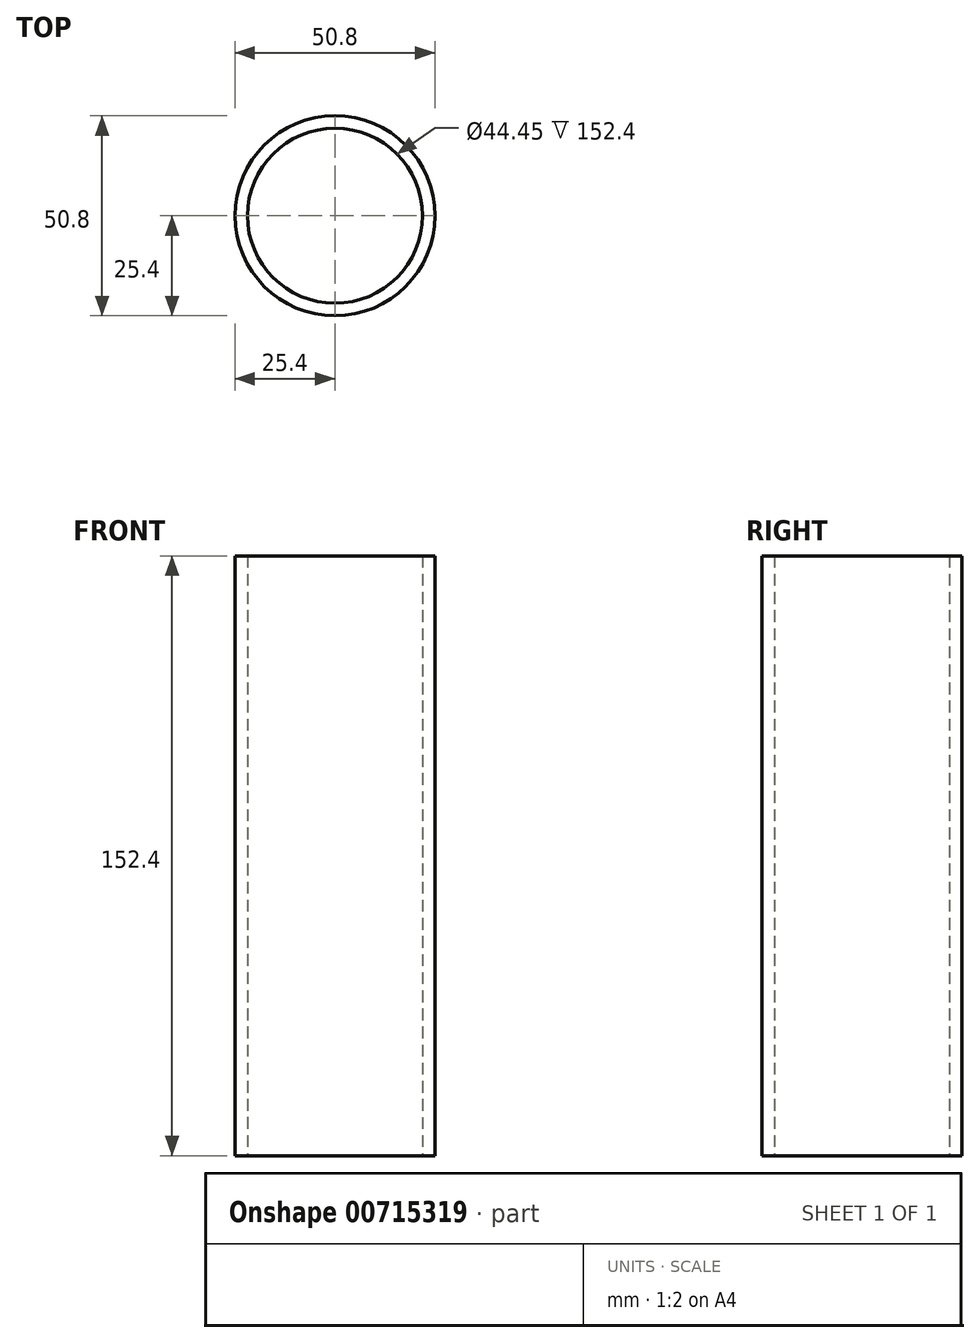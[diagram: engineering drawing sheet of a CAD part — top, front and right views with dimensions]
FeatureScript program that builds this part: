
annotation { "Feature Type Name" : "Feature", "Feature Type Description" : "" }
export const myFeature = defineFeature(function(context is Context, id is Id, definition is map)
    precondition{}
    {
        {
            var Q0;
            Q0=qCreatedBy(makeId("Top.planeOp"),FACE);
            var sketch = newSketch(context, id + "F0", { "sketchPlane" : qUnion([Q0])});
            skCircle(sketch, "E0", {"center": v(0, 0) * mm, "radius": 25.4 * mm});
            skCircle(sketch, "E1.0", {"center": v(0, 0) * mm, "radius": 22.23 * mm});
            skSolve(sketch);
        }
        {
            var Q0;
            Q0 = qSketchRegion(id + "F0", true);
            extrude(context, id + "F1", {"entities" : qUnion([Q0]), "depth" : 152.4 * mm, "offsetDistance" : 25.4 * mm});
        }
    });
